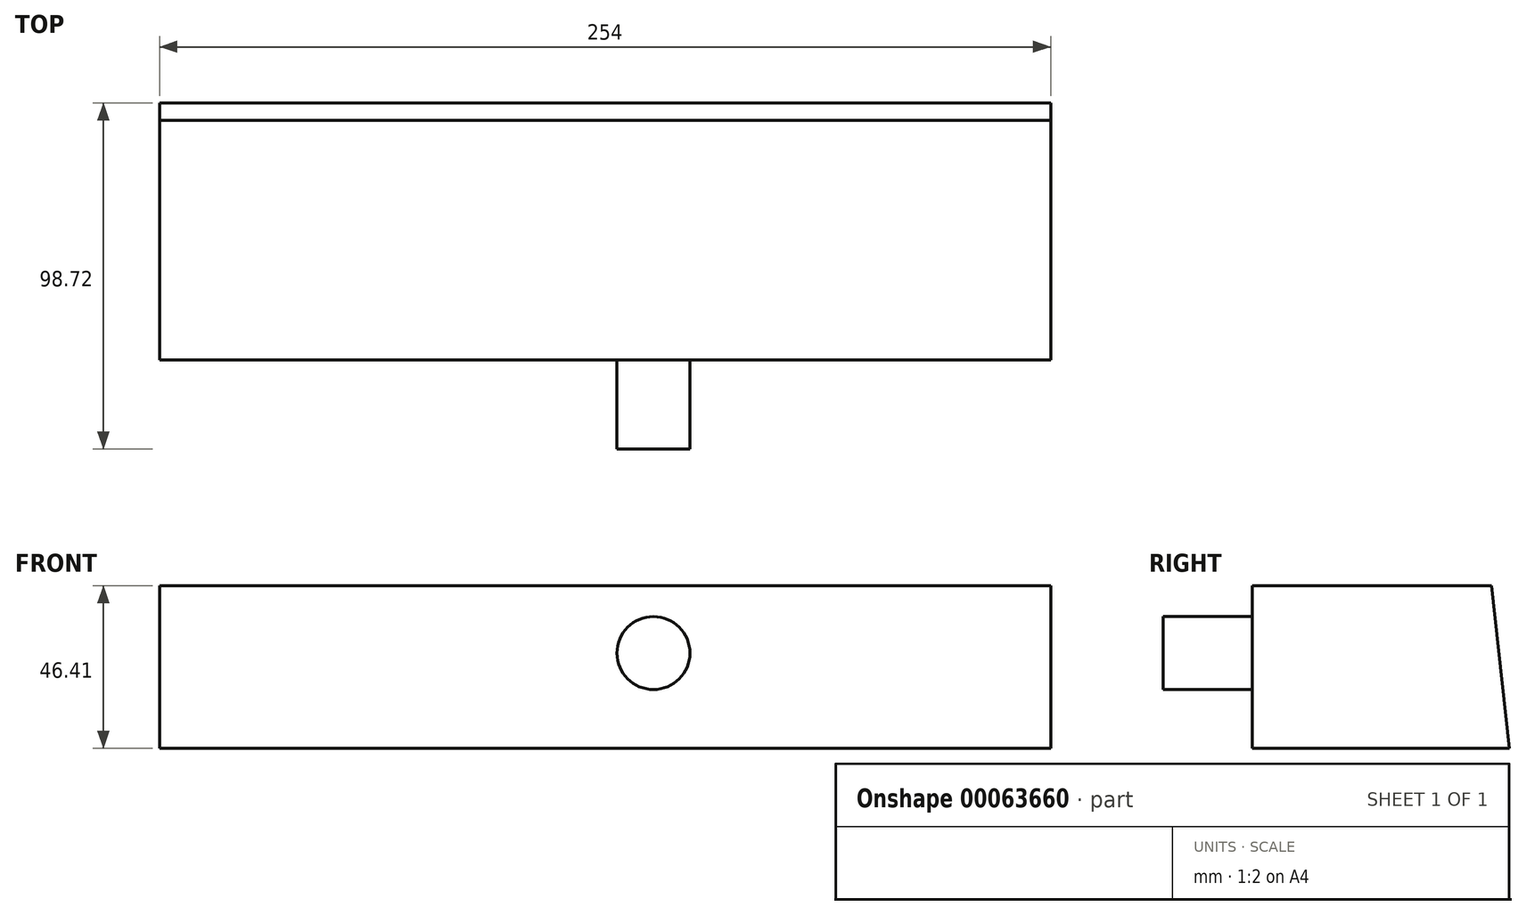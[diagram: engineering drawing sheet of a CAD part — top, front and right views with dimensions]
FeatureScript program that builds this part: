
annotation { "Feature Type Name" : "Feature", "Feature Type Description" : "" }
export const myFeature = defineFeature(function(context is Context, id is Id, definition is map)
    precondition{}
    {
        {
            var Q0;
            Q0=qCreatedBy(makeId("Right.planeOp"),FACE);
            var sketch = newSketch(context, id + "F0", { "sketchPlane" : qUnion([Q0])});
            skLineSegment(sketch, "E0", {"start": v(68.32, 46.41) * mm, "end": v(0, 46.41) * mm});
            skLineSegment(sketch, "E1", {"start": v(0, 46.41) * mm, "end": v(0, 0) * mm});
            skLineSegment(sketch, "E2", {"start": v(0, 0) * mm, "end": v(73.32, 0) * mm});
            skLineSegment(sketch, "E3", {"start": v(73.32, 0) * mm, "end": v(68.32, 46.41) * mm});
            skSolve(sketch);
        }
        {
            var Q0;
            Q0 = qSketchRegion(id + "F0", true);
            extrude(context, id + "F1", {"entities" : qUnion([Q0]), "depth" : 254 * mm});
        }
        {
            var Q0;
            Q0=makeQuery(id+"F1.opExtrude","SWEPT_FACE",FACE,{"disambiguationData":[OSD([sQuery(id+"F0.wireOp",EDGE,"E1")])]});
            var sketch = newSketch(context, id + "F2", { "sketchPlane" : qUnion([Q0])});
            skCircle(sketch, "E4", {"center": v(140.78, 27.21) * mm, "radius": 10.4 * mm});
            skSolve(sketch);
        }
        {
            var Q0;
            Q0 = qSketchRegion(id + "F2", true);
            extrude(context, id + "F3", {"entities" : qUnion([Q0]), "operationType" : NewBodyOperationType.ADD, "depth" : 25.4 * mm});
        }
    });
